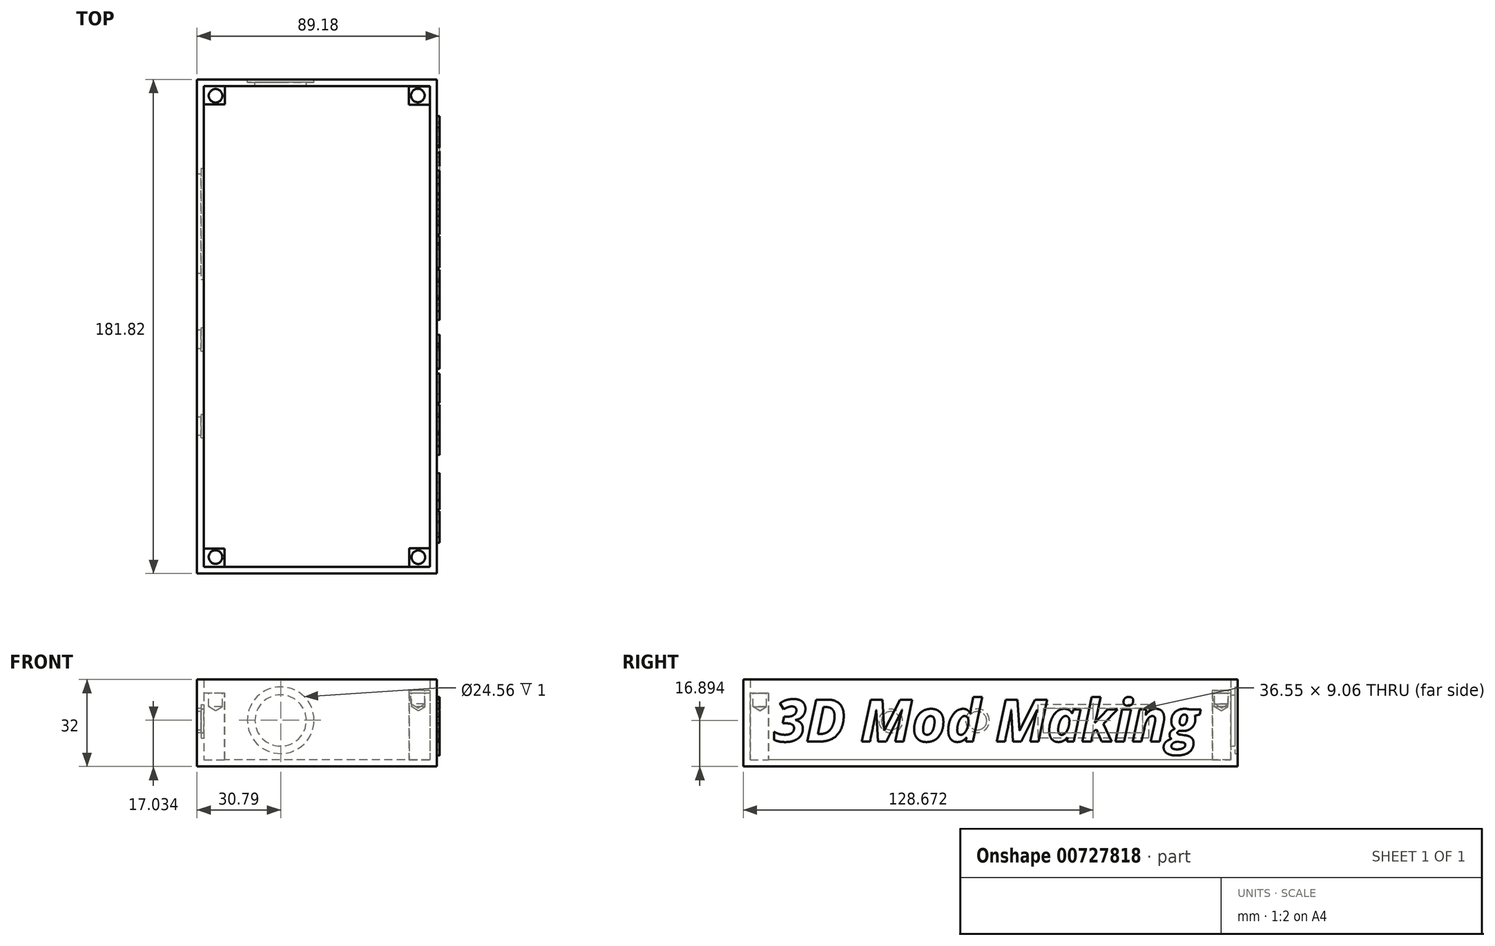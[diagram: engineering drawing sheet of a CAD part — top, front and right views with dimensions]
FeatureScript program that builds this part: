
annotation { "Feature Type Name" : "Feature", "Feature Type Description" : "" }
export const myFeature = defineFeature(function(context is Context, id is Id, definition is map)
    precondition{}
    {
        {
            var Q0;
            Q0=qCreatedBy(makeId("Top.planeOp"),FACE);
            var sketch = newSketch(context, id + "F0", { "sketchPlane" : qUnion([Q0])});
            skLineSegment(sketch, "E0.bottom", {"start": v(44.1, 90.91) * mm, "end": v(-44.1, 90.91) * mm});
            skLineSegment(sketch, "E0.top", {"start": v(44.1, -90.91) * mm, "end": v(-44.1, -90.91) * mm});
            skLineSegment(sketch, "E0.left", {"start": v(44.1, 90.91) * mm, "end": v(44.1, -90.91) * mm});
            skLineSegment(sketch, "E0.right", {"start": v(-44.1, 90.91) * mm, "end": v(-44.1, -90.91) * mm});
            skPoint(sketch, "E0.middle", {"position": v(0, 0) * mm});
            skSolve(sketch);
        }
        {
            var Q0;
            Q0 = qSketchRegion(id + "F0", true);
            extrude(context, id + "F1", {"entities" : qUnion([Q0]), "depth" : 32 * mm, "offsetDistance" : 25 * mm});
        }
        {
            var Q0;
            Q0=makeQuery(id+"F1.opExtrude","CAP_FACE",FACE,{"disambiguationData":[OSD([sQuery(id+"F0.wireOp",EDGE,"E0.bottom"),sQuery(id+"F0.wireOp",EDGE,"E0.top"),sQuery(id+"F0.wireOp",EDGE,"E0.left"),sQuery(id+"F0.wireOp",EDGE,"E0.right")])],"isStart":false});
            shell(context, id + "F2", {"entities" : qUnion([Q0]), "thickness" : 2.5 * mm});
        }
        {
            var Q0;
            Q0=qCreatedBy(makeId("Top.planeOp"),FACE);
            var sketch = newSketch(context, id + "F3", { "sketchPlane" : qUnion([Q0])});
            skLineSegment(sketch, "E1.bottom", {"start": v(41.57, 88.4) * mm, "end": v(33.87, 88.4) * mm});
            skLineSegment(sketch, "E1.top", {"start": v(41.57, 81.63) * mm, "end": v(33.87, 81.63) * mm});
            skLineSegment(sketch, "E1.left", {"start": v(41.57, 88.4) * mm, "end": v(41.57, 81.63) * mm});
            skLineSegment(sketch, "E1.right", {"start": v(33.87, 88.4) * mm, "end": v(33.87, 81.63) * mm});
            skSolve(sketch);
        }
        {
            var Q0;
            Q0 = qSketchRegion(id + "F3", true);
            extrude(context, id + "F4", {"entities" : qUnion([Q0]), "operationType" : NewBodyOperationType.ADD, "depth" : 28 * mm, "offsetDistance" : 25 * mm});
        }
        {
            var Q0;
            Q0=qCreatedBy(makeId("Top.planeOp"),FACE);
            var sketch = newSketch(context, id + "F5", { "sketchPlane" : qUnion([Q0])});
            skLineSegment(sketch, "E2.bottom", {"start": v(-33.9, 88.46) * mm, "end": v(-41.6, 88.46) * mm});
            skLineSegment(sketch, "E2.top", {"start": v(-33.9, 81.7) * mm, "end": v(-41.6, 81.7) * mm});
            skLineSegment(sketch, "E2.left", {"start": v(-33.9, 88.46) * mm, "end": v(-33.9, 81.7) * mm});
            skLineSegment(sketch, "E2.right", {"start": v(-41.6, 88.46) * mm, "end": v(-41.6, 81.7) * mm});
            skSolve(sketch);
        }
        {
            var Q0;
            Q0 = qSketchRegion(id + "F5", true);
            extrude(context, id + "F6", {"entities" : qUnion([Q0]), "operationType" : NewBodyOperationType.ADD, "depth" : 27 * mm, "offsetDistance" : 25 * mm});
        }
        {
            var Q0;
            Q0=qCreatedBy(makeId("Top.planeOp"),FACE);
            var sketch = newSketch(context, id + "F7", { "sketchPlane" : qUnion([Q0])});
            skLineSegment(sketch, "E3.bottom", {"start": v(-33.97, -81.7) * mm, "end": v(-41.67, -81.7) * mm});
            skLineSegment(sketch, "E3.top", {"start": v(-33.97, -88.47) * mm, "end": v(-41.67, -88.47) * mm});
            skLineSegment(sketch, "E3.left", {"start": v(-33.97, -81.7) * mm, "end": v(-33.97, -88.47) * mm});
            skLineSegment(sketch, "E3.right", {"start": v(-41.67, -81.7) * mm, "end": v(-41.67, -88.47) * mm});
            skSolve(sketch);
        }
        {
            var Q0;
            Q0 = qSketchRegion(id + "F7", true);
            extrude(context, id + "F8", {"entities" : qUnion([Q0]), "operationType" : NewBodyOperationType.ADD, "depth" : 27 * mm, "offsetDistance" : 25 * mm});
        }
        {
            var Q0;
            Q0=qCreatedBy(makeId("Top.planeOp"),FACE);
            var sketch = newSketch(context, id + "F9", { "sketchPlane" : qUnion([Q0])});
            skLineSegment(sketch, "E4.bottom", {"start": v(41.62, -81.63) * mm, "end": v(33.92, -81.63) * mm});
            skLineSegment(sketch, "E4.top", {"start": v(41.62, -88.4) * mm, "end": v(33.92, -88.4) * mm});
            skLineSegment(sketch, "E4.left", {"start": v(41.62, -81.63) * mm, "end": v(41.62, -88.4) * mm});
            skLineSegment(sketch, "E4.right", {"start": v(33.92, -81.63) * mm, "end": v(33.92, -88.4) * mm});
            skSolve(sketch);
        }
        {
            var Q0;
            Q0 = qSketchRegion(id + "F9", true);
            extrude(context, id + "F10", {"entities" : qUnion([Q0]), "operationType" : NewBodyOperationType.ADD, "depth" : 27 * mm, "offsetDistance" : 25 * mm});
        }
        {
            var Q0;
            Q0=makeQuery(id+"F4.opExtrude","CAP_FACE",FACE,{"disambiguationData":[OSD([sQuery(id+"F3.wireOp",EDGE,"E1.bottom"),sQuery(id+"F3.wireOp",EDGE,"E1.top"),sQuery(id+"F3.wireOp",EDGE,"E1.left"),sQuery(id+"F3.wireOp",EDGE,"E1.right")])],"isStart":false});
            var sketch = newSketch(context, id + "F11", { "sketchPlane" : qUnion([Q0])});
            skCircle(sketch, "E5", {"center": v(37.15, 85) * mm, "radius": 2.37 * mm});
            skSolve(sketch);
        }
        {
            var Q0;
            Q0=sQuery(id+"F11.wireOp",VERTEX,"E5.center");
            var Q1;
            Q1=makeQuery(id+"F1.opExtrude","SWEPT_BODY",BODY,{"disambiguationData":[OSD([sQuery(id+"F0.wireOp",EDGE,"E0.bottom"),sQuery(id+"F0.wireOp",EDGE,"E0.top"),sQuery(id+"F0.wireOp",EDGE,"E0.left"),sQuery(id+"F0.wireOp",EDGE,"E0.right")])]});
            hole(context, id + "F12", {"style" : HoleStyle.SIMPLE, "endStyle" : HoleEndStyle.BLIND, "holeDiameter" : 5 * mm, "majorDiameter" : 5 * mm, "holeDepth" : 5 * mm, "isTappedThrough" : true, "tappedDepth" : 12 * mm, "tapClearance" : 3, "locations" : qUnion([Q0]), "scope" : qUnion([Q1])});
        }
        {
            var Q0;
            Q0=makeQuery(id+"F10.opExtrude","CAP_FACE",FACE,{"disambiguationData":[OSD([sQuery(id+"F9.wireOp",EDGE,"E4.bottom"),sQuery(id+"F9.wireOp",EDGE,"E4.top"),sQuery(id+"F9.wireOp",EDGE,"E4.left"),sQuery(id+"F9.wireOp",EDGE,"E4.right")])],"isStart":false});
            var sketch = newSketch(context, id + "F13", { "sketchPlane" : qUnion([Q0])});
            skCircle(sketch, "E6", {"center": v(37.33, -84.9) * mm, "radius": 2.37 * mm});
            skSolve(sketch);
        }
        {
            var Q0;
            Q0=sQuery(id+"F13.wireOp",VERTEX,"E6.center");
            var Q1;
            Q1=makeQuery(id+"F1.opExtrude","SWEPT_BODY",BODY,{"disambiguationData":[OSD([sQuery(id+"F0.wireOp",EDGE,"E0.bottom"),sQuery(id+"F0.wireOp",EDGE,"E0.top"),sQuery(id+"F0.wireOp",EDGE,"E0.left"),sQuery(id+"F0.wireOp",EDGE,"E0.right")])]});
            hole(context, id + "F14", {"style" : HoleStyle.SIMPLE, "endStyle" : HoleEndStyle.BLIND, "holeDiameter" : 5 * mm, "majorDiameter" : 5 * mm, "holeDepth" : 5 * mm, "isTappedThrough" : true, "tappedDepth" : 12 * mm, "tapClearance" : 3, "locations" : qUnion([Q0]), "scope" : qUnion([Q1])});
        }
        {
            var Q0;
            Q0=makeQuery(id+"F8.opExtrude","CAP_FACE",FACE,{"disambiguationData":[OSD([sQuery(id+"F7.wireOp",EDGE,"E3.bottom"),sQuery(id+"F7.wireOp",EDGE,"E3.top"),sQuery(id+"F7.wireOp",EDGE,"E3.left"),sQuery(id+"F7.wireOp",EDGE,"E3.right")])],"isStart":false});
            var sketch = newSketch(context, id + "F15", { "sketchPlane" : qUnion([Q0])});
            skCircle(sketch, "E7", {"center": v(-37.29, -84.82) * mm, "radius": 2.37 * mm});
            skSolve(sketch);
        }
        {
            var Q0;
            Q0=sQuery(id+"F15.wireOp",VERTEX,"E7.center");
            var Q1;
            Q1=makeQuery(id+"F1.opExtrude","SWEPT_BODY",BODY,{"disambiguationData":[OSD([sQuery(id+"F0.wireOp",EDGE,"E0.bottom"),sQuery(id+"F0.wireOp",EDGE,"E0.top"),sQuery(id+"F0.wireOp",EDGE,"E0.left"),sQuery(id+"F0.wireOp",EDGE,"E0.right")])]});
            hole(context, id + "F16", {"style" : HoleStyle.SIMPLE, "endStyle" : HoleEndStyle.BLIND, "holeDiameter" : 5 * mm, "majorDiameter" : 5 * mm, "holeDepth" : 5 * mm, "isTappedThrough" : true, "tappedDepth" : 12 * mm, "tapClearance" : 3, "locations" : qUnion([Q0]), "scope" : qUnion([Q1])});
        }
        {
            var Q0;
            Q0=makeQuery(id+"F6.opExtrude","CAP_FACE",FACE,{"disambiguationData":[OSD([sQuery(id+"F5.wireOp",EDGE,"E2.bottom"),sQuery(id+"F5.wireOp",EDGE,"E2.top"),sQuery(id+"F5.wireOp",EDGE,"E2.left"),sQuery(id+"F5.wireOp",EDGE,"E2.right")])],"isStart":false});
            var sketch = newSketch(context, id + "F17", { "sketchPlane" : qUnion([Q0])});
            skCircle(sketch, "E8", {"center": v(-37.26, 84.89) * mm, "radius": 2.37 * mm});
            skSolve(sketch);
        }
        {
            var Q0;
            Q0=sQuery(id+"F17.wireOp",VERTEX,"E8.center");
            var Q1;
            Q1=makeQuery(id+"F1.opExtrude","SWEPT_BODY",BODY,{"disambiguationData":[OSD([sQuery(id+"F0.wireOp",EDGE,"E0.bottom"),sQuery(id+"F0.wireOp",EDGE,"E0.top"),sQuery(id+"F0.wireOp",EDGE,"E0.left"),sQuery(id+"F0.wireOp",EDGE,"E0.right")])]});
            hole(context, id + "F18", {"style" : HoleStyle.SIMPLE, "endStyle" : HoleEndStyle.BLIND, "holeDiameter" : 5 * mm, "majorDiameter" : 5 * mm, "holeDepth" : 5 * mm, "isTappedThrough" : true, "tappedDepth" : 12 * mm, "tapClearance" : 3, "locations" : qUnion([Q0]), "scope" : qUnion([Q1])});
        }
        {
            var Q0;
            Q0=makeQuery(id+"F2.opShell","OFFSET_FACE",FACE,{"disambiguationData":[OSD([sQuery(id+"F0.wireOp",EDGE,"E0.right")])]});
            var sketch = newSketch(context, id + "F19", { "sketchPlane" : qUnion([Q0])});
            skLineSegment(sketch, "E9.bottom", {"start": v(58.22, 22.8) * mm, "end": v(17.38, 22.8) * mm});
            skLineSegment(sketch, "E9.top", {"start": v(58.22, 10.52) * mm, "end": v(17.38, 10.52) * mm});
            skLineSegment(sketch, "E9.left", {"start": v(58.22, 22.8) * mm, "end": v(58.22, 10.52) * mm});
            skLineSegment(sketch, "E9.right", {"start": v(17.38, 22.8) * mm, "end": v(17.38, 10.52) * mm});
            skSolve(sketch);
        }
        {
            var Q0;
            Q0=makeQuery(id+"F19.imprint","IMPRINT",FACE,{"disambiguationData":[TD([[makeQuery(id+"F19.imprint","IMPRINT",EDGE,{"derivedFrom":sQuery(id+"F19.wireOp",EDGE,"E9.bottom")}),1.0]])]});
            extrude(context, id + "F20", {"entities" : qUnion([Q0]), "operationType" : NewBodyOperationType.REMOVE, "oppositeDirection" : true, "depth" : 1 * mm, "offsetDistance" : 25 * mm});
        }
        {
            var Q0;
            Q0=makeQuery(id+"F1.opExtrude","SWEPT_FACE",FACE,{"disambiguationData":[OSD([sQuery(id+"F0.wireOp",EDGE,"E0.right")])]});
            var sketch = newSketch(context, id + "F21", { "sketchPlane" : qUnion([Q0])});
            skLineSegment(sketch, "E10.bottom", {"start": v(-56.04, 12.36) * mm, "end": v(-19.49, 12.36) * mm});
            skLineSegment(sketch, "E10.top", {"start": v(-56.04, 21.42) * mm, "end": v(-19.49, 21.42) * mm});
            skLineSegment(sketch, "E10.left", {"start": v(-56.04, 12.36) * mm, "end": v(-56.04, 21.42) * mm});
            skLineSegment(sketch, "E10.right", {"start": v(-19.49, 12.36) * mm, "end": v(-19.49, 21.42) * mm});
            skSolve(sketch);
        }
        {
            var Q0;
            Q0 = qSketchRegion(id + "F21", true);
            extrude(context, id + "F22", {"entities" : qUnion([Q0]), "operationType" : NewBodyOperationType.REMOVE, "oppositeDirection" : true, "depth" : 2.5 * mm, "offsetDistance" : 25 * mm});
        }
        {
            var Q0;
            Q0=makeQuery(id+"F2.opShell","OFFSET_FACE",FACE,{"disambiguationData":[OSD([sQuery(id+"F0.wireOp",EDGE,"E0.right")])]});
            var sketch = newSketch(context, id + "F23", { "sketchPlane" : qUnion([Q0])});
            skCircle(sketch, "E11", {"center": v(-4.75, 16.86) * mm, "radius": 4.35 * mm});
            skSolve(sketch);
        }
        {
            var Q0;
            Q0=makeQuery(id+"F23.imprint","IMPRINT",FACE,{"disambiguationData":[TD([[makeQuery(id+"F23.imprint","IMPRINT",EDGE,{"derivedFrom":sQuery(id+"F23.wireOp",EDGE,"E11")}),1.0]])]});
            var sketch = newSketch(context, id + "F24", { "sketchPlane" : qUnion([Q0])});
            skCircle(sketch, "E12", {"center": v(-36.65, 16.75) * mm, "radius": 4.35 * mm});
            skSolve(sketch);
        }
        {
            var Q0;
            Q0 = qSketchRegion(id + "F24", true);
            var Q1;
            Q1 = qSketchRegion(id + "F23", true);
            extrude(context, id + "F25", {"entities" : qUnion([Q0, Q1]), "operationType" : NewBodyOperationType.REMOVE, "oppositeDirection" : true, "depth" : 1 * mm, "offsetDistance" : 25 * mm});
        }
        {
            var Q0;
            Q0=makeQuery(id+"F1.opExtrude","SWEPT_FACE",FACE,{"disambiguationData":[OSD([sQuery(id+"F0.wireOp",EDGE,"E0.right")])]});
            var sketch = newSketch(context, id + "F26", { "sketchPlane" : qUnion([Q0])});
            skCircle(sketch, "E13", {"center": v(36.68, 16.84) * mm, "radius": 3.4 * mm});
            skCircle(sketch, "E14", {"center": v(4.77, 16.84) * mm, "radius": 3.4 * mm});
            skSolve(sketch);
        }
        {
            var Q0;
            Q0 = qSketchRegion(id + "F26", true);
            extrude(context, id + "F27", {"entities" : qUnion([Q0]), "operationType" : NewBodyOperationType.REMOVE, "oppositeDirection" : true, "depth" : 2.5 * mm, "offsetDistance" : 25 * mm});
        }
        {
            var Q0;
            Q0=makeQuery(id+"F1.opExtrude","SWEPT_FACE",FACE,{"disambiguationData":[OSD([sQuery(id+"F0.wireOp",EDGE,"E0.bottom")])]});
            var sketch = newSketch(context, id + "F28", { "sketchPlane" : qUnion([Q0])});
            skCircle(sketch, "E15", {"center": v(13.3, 17.03) * mm, "radius": 12.28 * mm});
            skSolve(sketch);
        }
        {
            var Q0;
            Q0=makeQuery(id+"F28.imprint","IMPRINT",FACE,{"disambiguationData":[TD([[makeQuery(id+"F28.imprint","IMPRINT",EDGE,{"derivedFrom":sQuery(id+"F28.wireOp",EDGE,"E15")}),1.0]])]});
            extrude(context, id + "F29", {"entities" : qUnion([Q0]), "operationType" : NewBodyOperationType.REMOVE, "oppositeDirection" : true, "depth" : 1 * mm, "offsetDistance" : 25 * mm});
        }
        {
            var Q0;
            Q0 = qSketchRegion(id + "F28", true);
            var sketch = newSketch(context, id + "F30", { "sketchPlane" : qUnion([Q0])});
            skCircle(sketch, "E16", {"center": v(13.32, 16.92) * mm, "radius": 9.44 * mm});
            skSolve(sketch);
        }
        {
            var Q0;
            Q0 = qSketchRegion(id + "F30", true);
            extrude(context, id + "F31", {"entities" : qUnion([Q0]), "operationType" : NewBodyOperationType.REMOVE, "oppositeDirection" : true, "depth" : 2.5 * mm, "offsetDistance" : 25 * mm});
        }
        {
            var Q0;
            Q0=makeQuery(id+"F1.opExtrude","SWEPT_FACE",FACE,{"disambiguationData":[OSD([sQuery(id+"F0.wireOp",EDGE,"E0.left")])]});
            var sketch = newSketch(context, id + "F32", { "sketchPlane" : qUnion([Q0])});
            skText(sketch, "E17", { "text": "3D Mod Making", "fontName": "OpenSans-BoldItalic.ttf"});
            const initialGuessF32  = {"E17": [-0.07967, 0.00926, 1, 0, 0.01543]};
            skSetInitialGuess(sketch, initialGuessF32);
            skSolve(sketch);
        }
        {
            var Q0;
            Q0 = qSketchRegion(id + "F32", true);
            var Q1;
            Q1 = qBodyType(qCreatedBy(id + "F32" ,EDGE), BodyType.WIRE);
            extrude(context, id + "F33", {"entities" : qUnion([Q0]), "operationType" : NewBodyOperationType.ADD, "surfaceEntities" : qUnion([Q1]), "depth" : 1 * mm, "offsetDistance" : 25 * mm, "hasDraft" : true, "draftAngle" : 3 * degree});
        }
    });
